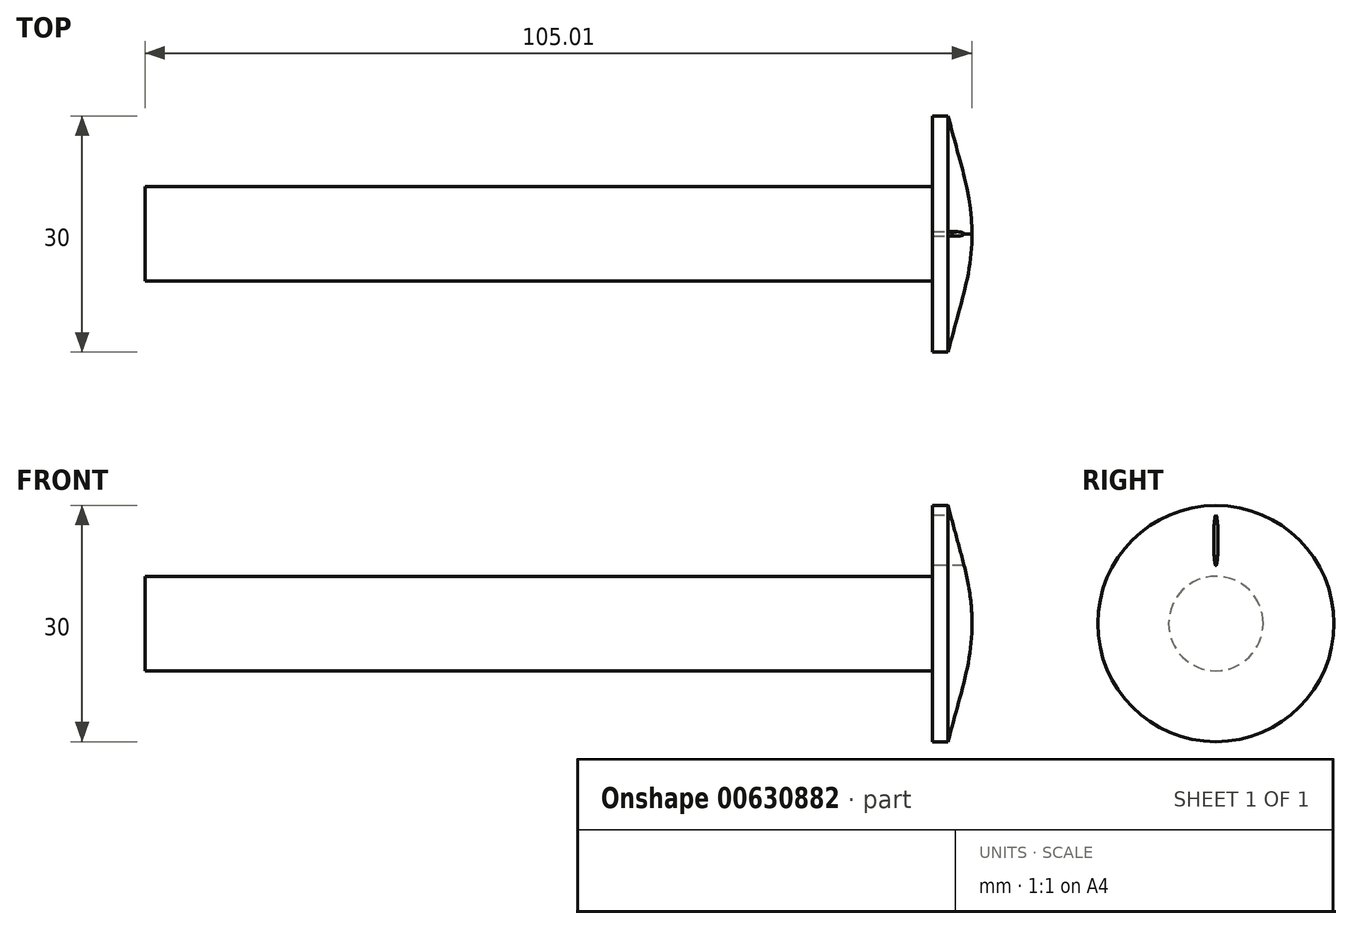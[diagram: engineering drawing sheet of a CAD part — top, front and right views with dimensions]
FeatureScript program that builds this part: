
annotation { "Feature Type Name" : "Feature", "Feature Type Description" : "" }
export const myFeature = defineFeature(function(context is Context, id is Id, definition is map)
    precondition{}
    {
        {
            var Q0;
            Q0=qCreatedBy(makeId("Front.planeOp"),FACE);
            var sketch = newSketch(context, id + "F0", { "sketchPlane" : qUnion([Q0])});
            skLineSegment(sketch, "E0.bottom", {"start": v(-11.57, 1.45) * mm, "end": v(88.43, 1.45) * mm});
            skLineSegment(sketch, "E0.top", {"start": v(-11.57, -4.55) * mm, "end": v(88.43, -4.55) * mm});
            skLineSegment(sketch, "E0.left", {"start": v(-11.57, 1.45) * mm, "end": v(-11.57, -4.55) * mm});
            skLineSegment(sketch, "E0.right", {"start": v(88.43, 1.45) * mm, "end": v(88.43, -4.55) * mm});
            skLineSegment(sketch, "E1", {"start": v(88.43, 1.45) * mm, "end": v(88.43, 10.45) * mm});
            skLineSegment(sketch, "E2", {"start": v(88.43, -4.55) * mm, "end": v(93.43, -4.55) * mm});
            skLineSegment(sketch, "E3", {"start": v(88.43, 10.45) * mm, "end": v(90.43, 10.45) * mm});
            skFitSpline(sketch, "E4", {"points": [v(90.43, 10.45) * mm, v(93.43, -4.55) * mm], "startDerivative": vector(4.11, -16.97) * mm, "endDerivative": vector(-0.42, -14.67) * mm});
            skLineSegment(sketch, "E5", {"start": v(-11.57, -4.55) * mm, "end": v(-17.62, -4.55) * mm});
            skSolve(sketch);
        }
        {
            var Q0;
            Q0=makeQuery(id+"F0.imprint","IMPRINT",FACE,{"disambiguationData":[TD([[makeQuery(id+"F0.imprint","IMPRINT",EDGE,{"derivedFrom":sQuery(id+"F0.wireOp",EDGE,"E0.right")}),1.0]])]});
            var Q1;
            Q1=makeQuery(id+"F0.imprint","IMPRINT",FACE,{"disambiguationData":[TD([[makeQuery(id+"F0.imprint","IMPRINT",EDGE,{"derivedFrom":sQuery(id+"F0.wireOp",EDGE,"E0.bottom")}),-1.0]])]});
            var Q2;
            Q2=sQuery(id+"F0.wireOp",EDGE,"E0.top");
            revolve(context, id + "F1", {"entities" : qUnion([Q0, Q1]), "axis" : qUnion([Q2]), "revolveType" : RevolveType.FULL});
        }
        {
            var Q0;
            Q0=qCreatedBy(makeId("Right.planeOp"),FACE);
            var sketch = newSketch(context, id + "F2", { "sketchPlane" : qUnion([Q0])});
            skEllipse(sketch, "E6", {"center": v(0, 6.04) * mm, "majorRadius": 3.2 * mm, "minorRadius": 0.27 * mm, "majorAxis": v(0, -1)});
            skSolve(sketch);
        }
        {
            var Q0;
            Q0=makeQuery(id+"F2.imprint","IMPRINT",FACE,{"disambiguationData":[TD([[makeQuery(id+"F2.imprint","IMPRINT",EDGE,{"derivedFrom":sQuery(id+"F2.wireOp",EDGE,"E6")}),1.0]])]});
            extrude(context, id + "F3", {"entities" : qUnion([Q0]), "operationType" : NewBodyOperationType.REMOVE, "depth" : 200 * mm, "offsetDistance" : 25 * mm});
        }
    });
